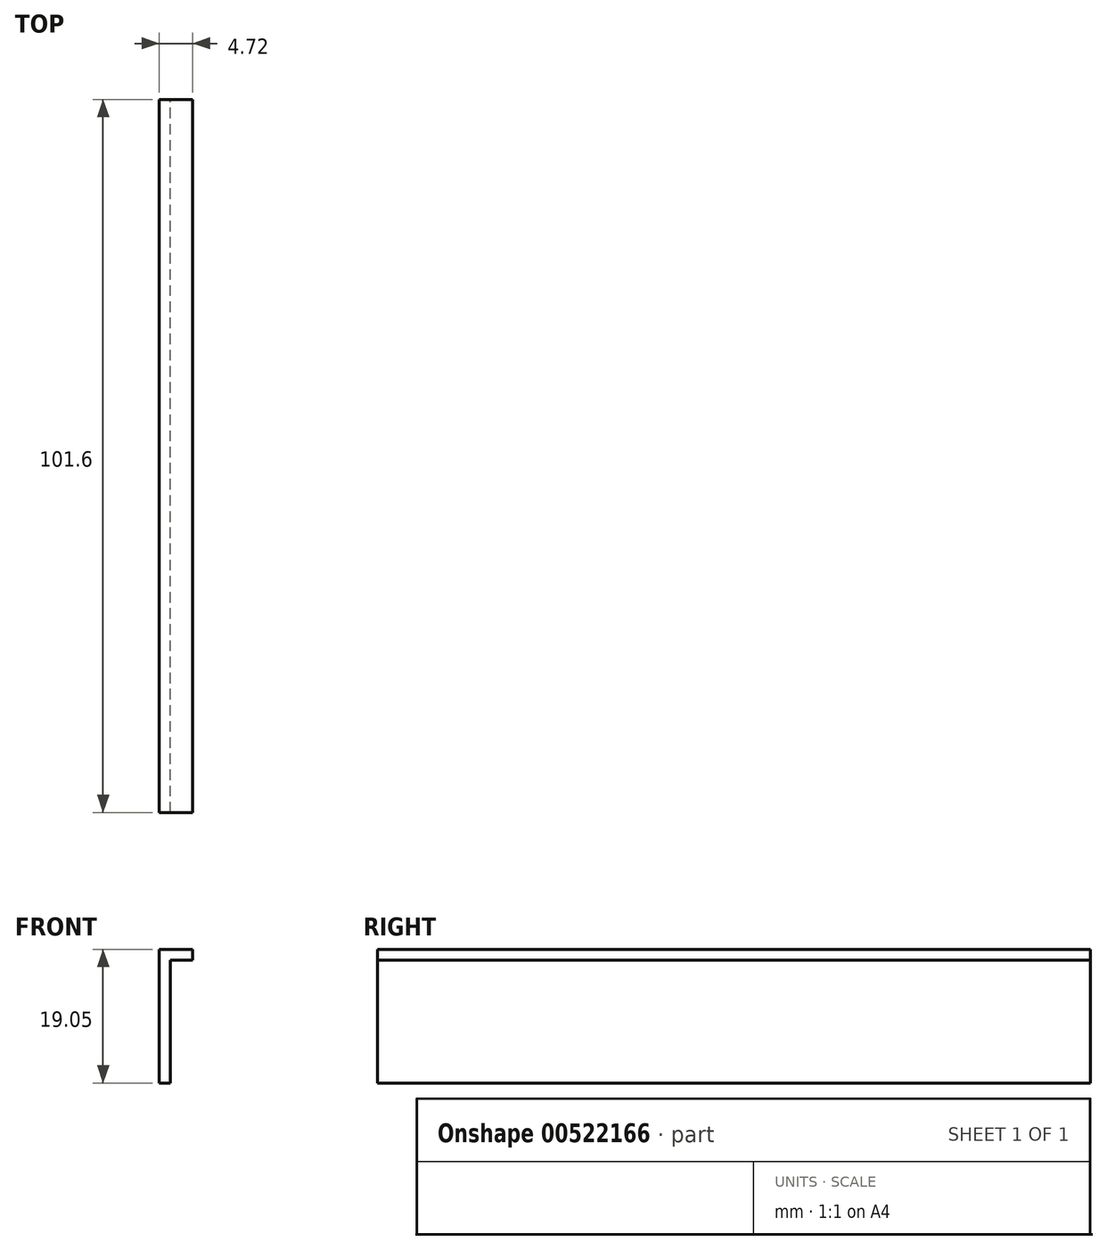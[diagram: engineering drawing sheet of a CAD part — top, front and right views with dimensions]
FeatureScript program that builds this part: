
annotation { "Feature Type Name" : "Feature", "Feature Type Description" : "" }
export const myFeature = defineFeature(function(context is Context, id is Id, definition is map)
    precondition{}
    {
        {
            var Q0;
            Q0=qCreatedBy(makeId("Front.planeOp"),FACE);
            var sketch = newSketch(context, id + "F0", { "sketchPlane" : qUnion([Q0])});
            skLineSegment(sketch, "E0", {"start": v(0, 0) * mm, "end": v(0, 19.05) * mm});
            skLineSegment(sketch, "E1", {"start": v(0, 19.05) * mm, "end": v(4.72, 19.05) * mm});
            skLineSegment(sketch, "E2", {"start": v(4.72, 19.05) * mm, "end": v(4.72, 17.48) * mm});
            skLineSegment(sketch, "E3", {"start": v(4.72, 17.48) * mm, "end": v(1.57, 17.48) * mm});
            skLineSegment(sketch, "E4", {"start": v(1.57, 17.48) * mm, "end": v(1.57, 0) * mm});
            skLineSegment(sketch, "E5", {"start": v(1.57, 0) * mm, "end": v(0, 0) * mm});
            skSolve(sketch);
        }
        {
            var Q0;
            Q0 = qSketchRegion(id + "F0", true);
            extrude(context, id + "F1", {"entities" : qUnion([Q0]), "depth" : 101.6 * mm, "offsetDistance" : 25.4 * mm});
        }
    });
